# Revit family: Drain_Floor-Jay R.Smith-Round-Type-DX2005-DX2010_Series
name_source: partatom
category: Plumbing Fixtures
units: mm (PartAtom-declared; Revit-internal decimal feet)

## family parameters
Always vertical = Yes
Cut with Voids When Loaded = No
OmniClass Number = 23.70.50.21.24
OmniClass Title = Waste Water Drains
Part Type = Normal
Room Calculation Point = No
Round Connector Dimension = Use Radius
Shared = No
Work Plane-Based = Yes

## types (6) — shared parameters
Adjustable Height = 1 1/4"
Adjustable Height Constraint = 1 1/4"
Assembly Code = D2030300
B - Sediment Bucket = No
CW Connection = No
Default Elevation = 0"
Description = FLOOR OR SHOWER DRAINS WITH ADJUSTABLE STRAINER HEADS
Diameter = 13"
Finish = Cast Iron-Jay R Smith-Duco Coated
G - Galvanized Cast Iron Body = No
HW Connection = No
Height = 5 1/4"
L - Speedi-Set Service Weight = No
LXH - Speedi-Set Extra Heavy = No
Load Rating = 'Light Duty having a Safe Live (Static) Load less than 2,000 lbs. (900 kg) per ASME A112.6.3 Floor Drain Standard.
Manufacturer = Jay R. Smith
Material = Cast Iron-Jay R Smith-Duco Coated
NB - Nickel Bronze Strainer = No
PB - Polished Bronze Strainer = No
Product Documentation Link = https://www.jrsmith.com
Quad Close Trap Seal = No
SH - Securing Holes = No
SS - Stainless Steel Strainers = No
Strainer Diameter = 5"
Strainer Radius = 2 1/2"
Strainer Width 5" = Yes
Strainer Width 6" = No
T - Threaded Outlet = No
Trap Primer Connection -P050   1/2" (13) & -P075 3/4" (19) = No
Type Comments = Round Top
U - Vandal Proof Screw = No
URL = http://www.jrsmith.com
Vent Connection = No
Waste Connection = Yes

## per-type parameters (varying)
| type | Connection Radius | Connection Size | Outlet Connection Description |
| DX 2005Y 02 | 1" | 2" | 2" No-HUB Outlet Connection |
| DX 2005Y 03 | 1 1/2" | 3" | 3" No-HUB Outlet Connection |
| DX 2005Y 04 | 2" | 4" | 4" No-HUB Outlet Connection |
| DX 2010C 02 | 1" | 2" | 2" Caulk Outlet Connection |
| DX 2010C 03 | 1 1/2" | 3" | 3" Caulk Outlet Connection |
| DX 2010C 04 | 2" | 4" | 4" Caulk Outlet Connection |

note: column(s) folded — value = type name in every type: Model

## geometry (parser evidence)
native form markers: Sweep x3
no freeform markers — native parametric forms only
